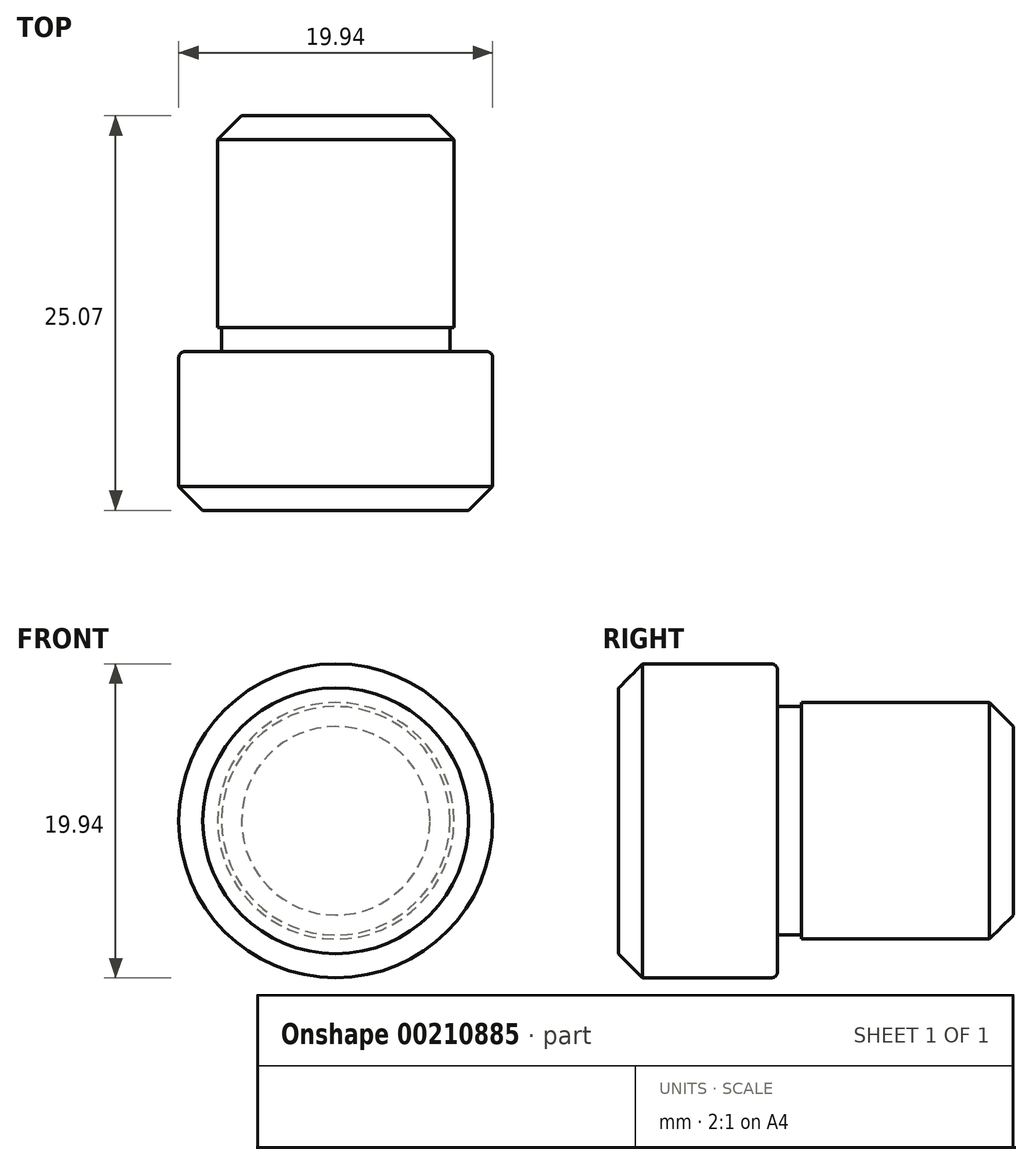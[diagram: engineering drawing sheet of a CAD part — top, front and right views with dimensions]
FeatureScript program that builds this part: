
annotation { "Feature Type Name" : "Feature", "Feature Type Description" : "" }
export const myFeature = defineFeature(function(context is Context, id is Id, definition is map)
    precondition{}
    {
        {
            var Q0;
            Q0=qCreatedBy(makeId("Right.planeOp"),FACE);
            var sketch = newSketch(context, id + "F0", { "sketchPlane" : qUnion([Q0])});
            skLineSegment(sketch, "E0", {"start": v(0, 0) * mm, "end": v(0, 7.51) * mm});
            skLineSegment(sketch, "E1", {"start": v(0, 7.51) * mm, "end": v(-13.46, 7.51) * mm});
            skLineSegment(sketch, "E2", {"start": v(-14.99, 7.51) * mm, "end": v(-14.99, 9.97) * mm});
            skLineSegment(sketch, "E3", {"start": v(-14.99, 9.97) * mm, "end": v(-25.07, 9.97) * mm});
            skLineSegment(sketch, "E4", {"start": v(-25.07, 9.97) * mm, "end": v(-25.07, 0) * mm});
            skLineSegment(sketch, "E5", {"start": v(-25.07, 0) * mm, "end": v(0, 0) * mm});
            skLineSegment(sketch, "E6", {"start": v(-14.99, 7.51) * mm, "end": v(-14.99, 7.26) * mm});
            skLineSegment(sketch, "E7", {"start": v(-14.99, 7.26) * mm, "end": v(-13.46, 7.26) * mm});
            skLineSegment(sketch, "E8", {"start": v(-13.46, 7.26) * mm, "end": v(-13.46, 7.51) * mm});
            skSolve(sketch);
        }
        {
            var Q0;
            Q0=makeQuery(id+"F0.imprint","IMPRINT",FACE,{"disambiguationData":[TD([[makeQuery(id+"F0.imprint","IMPRINT",EDGE,{"derivedFrom":sQuery(id+"F0.wireOp",EDGE,"E0")}),1.0]])]});
            var Q1;
            Q1=sQuery(id+"F0.wireOp",EDGE,"E5");
            revolve(context, id + "F1", {"entities" : qUnion([Q0]), "axis" : qUnion([Q1]), "revolveType" : RevolveType.FULL});
        }
        {
            var Q0;
            Q0=makeQuery(id+"F1.opRevolve","SWEPT_EDGE",EDGE,{"disambiguationData":[OSD([sQuery(id+"F0.wireOp",EDGE,"E3"),sQuery(id+"F0.wireOp",EDGE,"E4")])]});
            chamfer(context, id + "F2", {"entities" : qUnion([Q0]), "width" : 1.52 * mm, "tangentPropagation" : true});
        }
        {
            var Q0;
            Q0=makeQuery(id+"F1.opRevolve","SWEPT_EDGE",EDGE,{"disambiguationData":[OSD([sQuery(id+"F0.wireOp",EDGE,"E0"),sQuery(id+"F0.wireOp",EDGE,"E1")])]});
            chamfer(context, id + "F3", {"entities" : qUnion([Q0]), "width" : 1.52 * mm, "tangentPropagation" : true});
        }
        {
            var Q0;
            Q0=makeQuery(id+"F1.opRevolve","SWEPT_EDGE",EDGE,{"disambiguationData":[OSD([sQuery(id+"F0.wireOp",EDGE,"E2"),sQuery(id+"F0.wireOp",EDGE,"E3")])]});
            fillet(context, id + "F4", {"entities" : qUnion([Q0]), "radius" : 0.38 * mm, "tangentPropagation" : true, "allowEdgeOverflow" : false});
        }
    });
